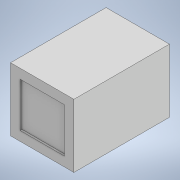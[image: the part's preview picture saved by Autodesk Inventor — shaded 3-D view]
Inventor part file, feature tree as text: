
AUTODESK INVENTOR PART (.ipt)
format: ipt  version: 2022.2 (Build 262287030, 287C)  size: 99,840 bytes
history: native  units: in
note: dims shown in document units (in); Inventor stores cm internally (conversion verified against a paired STEP export)
features: sketch x3, extrude x2
ambient origin geometry x8: Origin, YZ Plane, XZ Plane, XY Plane, X Axis, Y Axis, Z Axis, Center Point
bodies: Solid1 (feature_tree)
feature tree (5):
  extrude  "Extrusion1"  Depth=1.3189in
  extrude  "Extrusion2"  Depth=0.1969in
  sketch  "Sketch3"  dims[d5=0.1969in d6=0.0394in d7=0.0in]
  sketch  "Sketch1"  dims[d0=1.3189in d1=1.3189in]
  sketch  "Sketch2"  dims[d2=1.9882in d3=0.0in d4=0.1969in]
